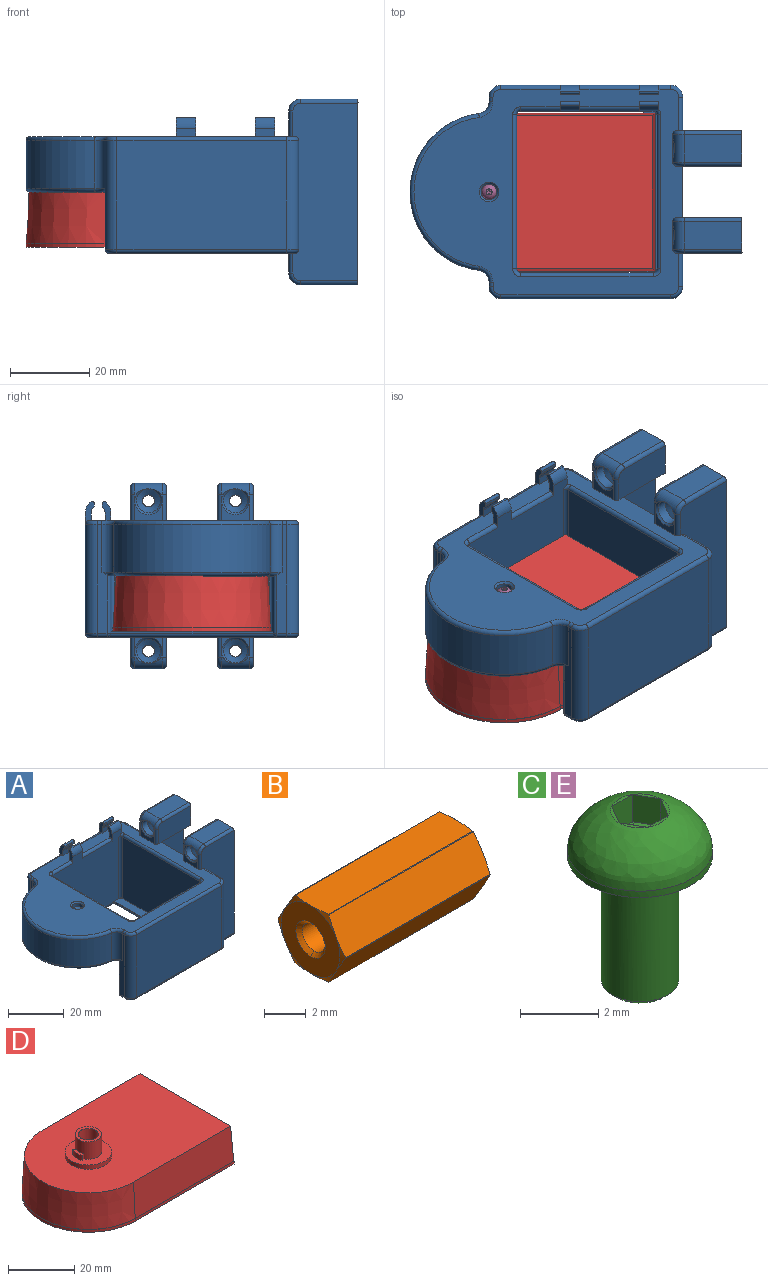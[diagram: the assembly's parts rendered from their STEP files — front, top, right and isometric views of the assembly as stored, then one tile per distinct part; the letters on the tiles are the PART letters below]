
ASSEMBLY  parts=5 mates=4
PART A: 200 faces, bbox 85.7x54.5x47.5 mm
  f0: plane 43x30.5mm, normal (0,1,0), area 1212.5mm2, adj f1,f5,f6,f10,f21,f25,f26,f29
  f1: cylinder r=3.25mm len=5mm, axis (1,0,0), area 16.2mm2, adj f0,f5,f6,f7
  f2: plane 5x0.63mm, normal (0,-1,0), area 3.1mm2, adj f5,f6,f7,f8
  f3: cylinder r=1.75mm len=5mm, axis (1,0,0), area 7.4mm2, adj f4,f5,f6,f8
  f4: plane 5x2mm, normal (0,-1,0), area 10mm2, adj f3,f5,f6,f9
  f5: plane 5.81x2.25mm, normal (-1,0,0), area 7.4mm2, adj f0,f1,f2,f3,f4,f7,f8,f9
  f6: plane 5.81x2.25mm, normal (1,0,0), area 7.4mm2, adj f0,f1,f2,f3,f4,f7,f8,f9
  f7: cylinder r=0.5mm len=5mm, axis (1,0,0), area 5.4mm2, adj f1,f2,f5,f6
  f8: cylinder r=0.5mm len=5mm, axis (1,0,0), area 2.1mm2, adj f2,f3,f5,f6
  f9: plane 68x52mm, normal (0,0,1), area 1399.2mm2, adj f4,f5,f6,f10,f14,f16,f17,f20
  f10: cylinder r=1mm len=15mm, axis (1,0,0), area 23.6mm2, adj f0,f5,f9,f128
  f11: plane 5x0.63mm, normal (0,1,0), area 3.1mm2, adj f16,f17,f18,f19
  f12: cylinder r=3.25mm len=5mm, axis (1,0,0), area 16.2mm2, adj f13,f16,f17,f18
  f13: plane 42x30.5mm, normal (0,-1,0), area 1050.6mm2, adj f12,f16,f17,f20,f31,f34,f35,f38
  f14: plane 5x2mm, normal (0,1,0), area 10mm2, adj f9,f15,f16,f17
  f15: cylinder r=1.75mm len=5mm, axis (1,0,0), area 7.4mm2, adj f14,f16,f17,f19
  f16: plane 5.81x2.25mm, normal (-1,0,0), area 7.4mm2, adj f9,f11,f12,f13,f14,f15,f18,f19
  f17: plane 5.81x2.25mm, normal (1,0,0), area 7.4mm2, adj f9,f11,f12,f13,f14,f15,f18,f19
  f18: cylinder r=0.5mm len=5mm, axis (1,0,0), area 5.4mm2, adj f11,f12,f16,f17
  f19: cylinder r=0.5mm len=5mm, axis (1,0,0), area 2.1mm2, adj f11,f15,f16,f17
  f20: cylinder r=1mm len=10mm, axis (-1,0,0), area 15.7mm2, adj f9,f13,f16,f177
  f21: cylinder r=3.25mm len=5mm, axis (1,0,0), area 16.2mm2, adj f0,f25,f26,f27
  f22: plane 5x0.63mm, normal (0,-1,0), area 3.1mm2, adj f25,f26,f27,f28
  f23: cylinder r=1.75mm len=5mm, axis (1,0,0), area 7.4mm2, adj f24,f25,f26,f28
  f24: plane 5x2mm, normal (0,-1,0), area 10mm2, adj f9,f23,f25,f26
  f25: plane 5.81x2.25mm, normal (-1,0,0), area 7.4mm2, adj f0,f9,f21,f22,f23,f24,f27,f28
  f26: plane 5.81x2.25mm, normal (1,0,0), area 7.4mm2, adj f0,f9,f21,f22,f23,f24,f27,f28
  f27: cylinder r=0.5mm len=5mm, axis (1,0,0), area 5.4mm2, adj f21,f22,f25,f26
  f28: cylinder r=0.5mm len=5mm, axis (1,0,0), area 2.1mm2, adj f22,f23,f25,f26
  f29: cylinder r=1mm len=15mm, axis (1,0,0), area 23.6mm2, adj f0,f6,f9,f25
  f30: plane 5x0.63mm, normal (0,1,0), area 3.1mm2, adj f34,f35,f36,f37
  f31: cylinder r=3.25mm len=5mm, axis (1,0,0), area 16.2mm2, adj f13,f34,f35,f36
  f32: plane 5x2mm, normal (0,1,0), area 10mm2, adj f9,f33,f34,f35
  f33: cylinder r=1.75mm len=5mm, axis (1,0,0), area 7.4mm2, adj f32,f34,f35,f37
  f34: plane 5.81x2.25mm, normal (-1,0,0), area 7.4mm2, adj f9,f13,f30,f31,f32,f33,f36,f37
  f35: plane 4.84x2.27mm, normal (1,0,0), area 7.2mm2, adj f9,f13,f30,f31,f32,f33,f36,f37
  f36: cylinder r=0.5mm len=5mm, axis (1,0,0), area 5.4mm2, adj f30,f31,f34,f35
  f37: cylinder r=0.5mm len=5mm, axis (1,0,0), area 2.1mm2, adj f30,f33,f34,f35
  f38: cylinder r=1mm len=15mm, axis (-1,0,0), area 23.6mm2, adj f9,f13,f17,f34
  f39: cylinder r=1.5mm len=13.6mm, axis (1,0,0), area 128.2mm2, adj f68,f197
  f40: plane 1.5x0.34mm, normal (-1,0,0), area 0.2mm2, adj f43,f150,f199
  f41: plane 3.5x3.5mm, normal (-1,0,0), area 2.6mm2, adj f76,f150,f199
  f42: plane 1.5x0.34mm, normal (-1,0,0), area 0.2mm2, adj f43,f153,f199
  f43: cylinder r=3mm len=7mm, axis (0,-1,0), area 25.5mm2, adj f40,f42,f101,f149,f152,f199
  f44: cylinder r=1.5mm len=13.6mm, axis (1,0,0), area 128.2mm2, adj f71,f196
  f45: plane 1.5x0.34mm, normal (-1,0,0), area 0.2mm2, adj f48,f135,f195
  f46: plane 3.5x3.5mm, normal (-1,0,0), area 2.6mm2, adj f76,f135,f195
  f47: plane 1.5x0.34mm, normal (-1,0,0), area 0.2mm2, adj f48,f132,f195
  f48: cylinder r=3mm len=7mm, axis (0,-1,0), area 25.5mm2, adj f45,f47,f93,f131,f134,f195
  f49: cylinder r=1.5mm len=13.6mm, axis (1,0,0), area 128.2mm2, adj f68,f193
  f50: plane 1.5x0.34mm, normal (-1,0,0), area 0.2mm2, adj f52,f144,f192
  f51: plane 7x5mm, normal (-1,0,0), area 15.8mm2, adj f9,f144,f147,f192
  f52: cylinder r=3mm len=7mm, axis (0,1,0), area 25.5mm2, adj f50,f107,f108,f143,f146,f192
  f53: cylinder r=1.5mm len=13.6mm, axis (1,0,0), area 128.2mm2, adj f71,f188
  f54: plane 1.5x0.34mm, normal (-1,0,0), area 0.2mm2, adj f56,f141,f190
  f55: plane 7x5mm, normal (-1,0,0), area 15.8mm2, adj f9,f138,f141,f190
  f56: cylinder r=3mm len=7mm, axis (0,1,0), area 25.5mm2, adj f54,f99,f100,f137,f140,f190
  f57: cylinder r=1mm len=2mm, axis (0,0,-1), area 8.8mm2, adj f92,f187
  f58: plane 29.5x20mm, normal (1,0,0), area 579.5mm2, adj f9,f69,f70,f76,f95,f96,f98,f103
  f59: plane 4.2x1.37mm, normal (0,0,-1), area 3.9mm2, adj f81,f82,f83,f84
  f60: plane 39x13mm, normal (1,0,0), area 484.6mm2, adj f61,f77,f79,f80,f170,f176,f178
  f61: plane 41.4x27mm, normal (0,0,-1), area 681.3mm2, adj f13,f60,f75,f77,f78,f79,f164,f165
  f62: plane 27.54x2.54mm, normal (-1,0,0), area 52.6mm2, adj f111,f116,f129,f154,f166,f182
  f63: cylinder r=20mm len=39.66mm, axis (0,0,-1), area 691.2mm2, adj f111,f112,f125,f165
  f64: plane 27.54x2.54mm, normal (-1,0,0), area 52.6mm2, adj f112,f113,f121,f159,f164,f179
  f65: plane 43x27.5mm, normal (0,-1,0), area 1182.5mm2, adj f113,f114,f119,f162
  f66: plane 27.5x8.5mm, normal (1,0,0), area 233.7mm2, adj f67,f114,f117,f161
  f67: plane 45x16.5mm, normal (0,-1,0), area 697mm2, adj f9,f66,f68,f76,f117,f145,f146,f147
  f68: plane 47x9mm, normal (1,0,0), area 310mm2, adj f39,f49,f67,f69,f101,f103,f104,f105
  f69: plane 28x15mm, normal (0,1,0), area 420mm2, adj f58,f68,f104,f105
  f70: plane 28x15mm, normal (0,-1,0), area 420mm2, adj f58,f71,f96,f98
  f71: plane 47x9mm, normal (1,0,0), area 310mm2, adj f44,f53,f70,f72,f93,f95,f96,f97
  f72: plane 45x16.5mm, normal (0,1,0), area 697mm2, adj f9,f71,f73,f76,f122,f133,f134,f135
  f73: plane 27.5x8.5mm, normal (1,0,0), area 233.7mm2, adj f72,f115,f122,f157
  f74: plane 39x27mm, normal (-1,0,0), area 1053mm2, adj f110,f168,f172,f173
  f75: plane 40.5x27.5mm, normal (0,1,0), area 1021.5mm2, adj f61,f109,f110,f168,f170,f171,f179,f181
  f76: plane 52x48mm, normal (0,0,-1), area 750.4mm2, adj f41,f46,f58,f67,f72,f94,f95,f102
  f77: plane 7x1.6mm, normal (0,-1,0), area 11.2mm2, adj f60,f61,f78,f80
  f78: cylinder r=7mm len=14mm, axis (0,0,-1), area 35.2mm2, adj f61,f77,f79,f80
  f79: plane 7x1.6mm, normal (0,1,0), area 11.2mm2, adj f60,f61,f78,f80
  f80: plane 14x14mm, normal (0,0,-1), area 120.8mm2, adj f60,f77,f78,f79,f81,f82,f83,f84
  f81: plane 1.9x0.91mm, normal (-0.42,0.91,0), area 1.9mm2, adj f59,f80,f82,f84
  f82: cylinder r=4mm len=8mm, axis (0,0,-1), area 154.3mm2, adj f59,f80,f81,f83,f85
  f83: plane 1.9x0.91mm, normal (-0.42,-0.91,0), area 1.9mm2, adj f59,f80,f82,f84
  f84: cylinder r=5mm len=4.2mm, axis (0,0,-1), area 8.2mm2, adj f59,f80,f81,f83
  f85: plane 8x8mm, normal (0,0,-1), area 32.7mm2, adj f82,f86,f87,f88,f89,f90,f91
  f86: plane 2.13x2mm, normal (-0.82,0.57,0), area 5.2mm2, adj f85,f87,f91,f92
  f87: plane 2.35x2mm, normal (-0.91,-0.42,0), area 5.2mm2, adj f85,f86,f88,f92
  f88: plane 2.59x2mm, normal (-0.09,-1,0), area 5.2mm2, adj f85,f87,f89,f92
  f89: plane 2.13x2mm, normal (0.82,-0.57,0), area 5.2mm2, adj f85,f88,f90,f92
  f90: plane 2.35x2mm, normal (0.91,0.42,0), area 5.2mm2, adj f85,f89,f91,f92
  f91: plane 2.59x2mm, normal (0.09,1,0), area 5.2mm2, adj f85,f86,f90,f92
  f92: plane 5.18x4.71mm, normal (0,0,-1), area 14.4mm2, adj f57,f86,f87,f88,f89,f90,f91
  f93: plane 14.5x7mm, normal (0,0,-1), area 101.5mm2, adj f48,f71,f130,f133
  f94: plane 3.5x3.5mm, normal (-1,0,0), area 2.6mm2, adj f76,f132,f195
  f95: plane 16.5x8.5mm, normal (0,-1,0), area 137.1mm2, adj f58,f71,f76,f96,f130,f131,f132
  f96: plane 15x3.5mm, normal (0,0,1), area 52.5mm2, adj f58,f70,f71,f95
  f97: plane 16.5x8.5mm, normal (0,-1,0), area 139.4mm2, adj f9,f71,f98,f136,f137,f138
  f98: plane 15x3.5mm, normal (0,0,-1), area 52.5mm2, adj f58,f70,f71,f97
  f99: plane 14.5x7mm, normal (0,0,1), area 101.5mm2, adj f56,f71,f136,f139
  f100: plane 1.5x0.34mm, normal (-1,0,0), area 0.2mm2, adj f56,f138,f190
  f101: plane 14.5x7mm, normal (0,0,-1), area 101.5mm2, adj f43,f68,f148,f151
  f102: plane 3.5x3.5mm, normal (-1,0,0), area 2.6mm2, adj f76,f153,f199
  f103: plane 16.5x8.5mm, normal (0,1,0), area 137.1mm2, adj f58,f68,f76,f104,f148,f149,f150
  f104: plane 15x3.5mm, normal (0,0,1), area 52.5mm2, adj f58,f68,f69,f103
  f105: plane 15x3.5mm, normal (0,0,-1), area 52.5mm2, adj f58,f68,f69,f106
  f106: plane 16.5x8.5mm, normal (0,1,0), area 139.4mm2, adj f9,f68,f105,f142,f143,f144
  f107: plane 14.5x7mm, normal (0,0,1), area 101.5mm2, adj f52,f68,f142,f145
  f108: plane 1.5x0.34mm, normal (-1,0,0), area 0.2mm2, adj f52,f147,f192
  f109: plane 41x0.5mm, normal (-1,0,0), area 20.5mm2, adj f13,f75,f110,f167
  f110: plane 41x3.5mm, normal (0,0,1), area 143.1mm2, adj f13,f74,f75,f109,f168,f173
  f111: cylinder r=3mm len=12mm, axis (0,0,-1), area 51.8mm2, adj f62,f63,f127,f166
  f112: cylinder r=3mm len=12mm, axis (0,0,-1), area 51.8mm2, adj f63,f64,f123,f164
  f113: cylinder r=3mm len=27.5mm, axis (0,0,-1), area 129.6mm2, adj f64,f65,f120,f160
  f114: cylinder r=3mm len=27.5mm, axis (0,0,-1), area 129.6mm2, adj f65,f66,f118,f163
  f115: cylinder r=3mm len=27.5mm, axis (0,0,-1), area 129.6mm2, adj f0,f73,f124,f158
  f116: cylinder r=3mm len=27.5mm, axis (0,0,-1), area 129.6mm2, adj f0,f62,f128,f155
  f117: cylinder r=1mm len=8.5mm, axis (0,-1,0), area 13.4mm2, adj f9,f66,f67,f118
  f118: torus R=2mm, axis (0,0,1), area 6.5mm2, adj f9,f114,f117,f119
  f119: cylinder r=1mm len=43mm, axis (-1,0,0), area 67.5mm2, adj f9,f65,f118,f120
  f120: torus R=2mm, axis (0,0,1), area 6.5mm2, adj f9,f113,f119,f121
  f121: cylinder r=1mm len=1.2mm, axis (0,1,0), area 1.9mm2, adj f9,f64,f120,f123
  f122: cylinder r=1mm len=8.5mm, axis (0,-1,0), area 13.4mm2, adj f9,f72,f73,f124
  f123: torus R=4mm, axis (0,0,1), area 7.6mm2, adj f9,f112,f121,f125
  f124: torus R=2mm, axis (0,0,1), area 6.5mm2, adj f9,f115,f122,f126
  f125: torus R=19mm, axis (0,0,1), area 88.8mm2, adj f9,f63,f123,f127
  f126: cylinder r=1mm len=3mm, axis (1,0,0), area 4.7mm2, adj f0,f9,f26,f124
  f127: torus R=4mm, axis (0,0,1), area 7.6mm2, adj f9,f111,f125,f129
  f128: torus R=2mm, axis (0,0,1), area 6.5mm2, adj f9,f10,f116,f129
  f129: cylinder r=1mm len=1.2mm, axis (0,1,0), area 1.9mm2, adj f9,f62,f127,f128
  f130: cylinder r=1mm len=14.5mm, axis (-1,0,0), area 22.8mm2, adj f71,f93,f95,f131
  f131: torus R=2mm, axis (0,-1,0), area 6.5mm2, adj f48,f95,f130,f132
  f132: cylinder r=1mm len=5mm, axis (0,0,1), area 7.9mm2, adj f47,f76,f94,f95,f131
  f133: cylinder r=1mm len=14.5mm, axis (-1,0,0), area 22.8mm2, adj f71,f72,f93,f134
  f134: torus R=2mm, axis (0,1,0), area 6.5mm2, adj f48,f72,f133,f135
  f135: cylinder r=1mm len=5mm, axis (0,0,-1), area 7.9mm2, adj f45,f46,f72,f76,f134
  f136: cylinder r=1mm len=14.5mm, axis (-1,0,0), area 22.8mm2, adj f71,f97,f99,f137
  f137: torus R=2mm, axis (0,1,0), area 6.5mm2, adj f56,f97,f136,f138
  f138: cylinder r=1mm len=6.5mm, axis (0,0,1), area 10.2mm2, adj f9,f55,f97,f100,f137
  f139: cylinder r=1mm len=14.5mm, axis (1,0,0), area 22.8mm2, adj f71,f72,f99,f140
  f140: torus R=2mm, axis (0,1,0), area 6.5mm2, adj f56,f72,f139,f141
  f141: cylinder r=1mm len=6.5mm, axis (0,0,-1), area 10.2mm2, adj f9,f54,f55,f72,f140
  f142: cylinder r=1mm len=14.5mm, axis (-1,0,0), area 22.8mm2, adj f68,f106,f107,f143
  f143: torus R=2mm, axis (0,1,0), area 6.5mm2, adj f52,f106,f142,f144
  f144: cylinder r=1mm len=6.5mm, axis (0,0,-1), area 10.2mm2, adj f9,f50,f51,f106,f143
  f145: cylinder r=1mm len=14.5mm, axis (1,0,0), area 22.8mm2, adj f67,f68,f107,f146
  f146: torus R=2mm, axis (0,1,0), area 6.5mm2, adj f52,f67,f145,f147
  f147: cylinder r=1mm len=6.5mm, axis (0,0,-1), area 10.2mm2, adj f9,f51,f67,f108,f146
  f148: cylinder r=1mm len=14.5mm, axis (-1,0,0), area 22.8mm2, adj f68,f101,f103,f149
  f149: torus R=2mm, axis (0,-1,0), area 6.5mm2, adj f43,f103,f148,f150
  f150: cylinder r=1mm len=5mm, axis (0,0,-1), area 7.9mm2, adj f40,f41,f76,f103,f149
  f151: cylinder r=1mm len=14.5mm, axis (-1,0,0), area 22.8mm2, adj f67,f68,f101,f152
  f152: torus R=2mm, axis (0,1,0), area 6.5mm2, adj f43,f67,f151,f153
  f153: cylinder r=1mm len=5mm, axis (0,0,-1), area 7.9mm2, adj f42,f67,f76,f102,f152
  f154: cylinder r=1mm len=2.5mm, axis (0,-1,0), area 3.9mm2, adj f62,f76,f155,f183
  f155: torus R=2mm, axis (0,0,1), area 6.5mm2, adj f76,f116,f154,f156
  f156: cylinder r=1mm len=43mm, axis (-1,0,0), area 67.5mm2, adj f0,f76,f155,f158
  f157: cylinder r=1mm len=8.5mm, axis (0,1,0), area 13.4mm2, adj f72,f73,f76,f158
  f158: torus R=2mm, axis (0,0,1), area 6.5mm2, adj f76,f115,f156,f157
  f159: cylinder r=1mm len=2.5mm, axis (0,-1,0), area 3.9mm2, adj f64,f76,f160,f180
  f160: torus R=2mm, axis (0,0,1), area 6.5mm2, adj f76,f113,f159,f162
  f161: cylinder r=1mm len=8.5mm, axis (0,1,0), area 13.4mm2, adj f66,f67,f76,f163
  f162: cylinder r=1mm len=43mm, axis (1,0,0), area 67.5mm2, adj f65,f76,f160,f163
  f163: torus R=2mm, axis (0,0,1), area 6.5mm2, adj f76,f114,f161,f162
  f164: torus R=4mm, axis (0,0,1), area 5.6mm2, adj f61,f64,f112,f165,f179
  f165: torus R=19mm, axis (0,0,1), area 88.8mm2, adj f61,f63,f164,f166
  f166: torus R=4mm, axis (0,0,1), area 5.6mm2, adj f61,f62,f111,f165,f182
  f167: cylinder r=1mm len=43mm, axis (0,1,0), area 65.5mm2, adj f76,f109,f181,f184
  f168: cylinder r=1mm len=27mm, axis (0,0,-1), area 42.4mm2, adj f74,f75,f110,f169
  f169: torus R=2mm, axis (0,0,1), area 3.4mm2, adj f9,f168,f171,f172
  f170: cylinder r=1mm len=13mm, axis (0,0,1), area 20.4mm2, adj f60,f61,f75,f174
  f171: cylinder r=1mm len=33.5mm, axis (1,0,0), area 52.6mm2, adj f9,f75,f169,f174
  f172: cylinder r=1mm len=39mm, axis (0,1,0), area 61.3mm2, adj f9,f74,f169,f175
  f173: cylinder r=1mm len=27mm, axis (0,0,1), area 42.4mm2, adj f13,f74,f110,f175
  f174: torus R=2mm, axis (0,0,1), area 3.4mm2, adj f9,f170,f171,f176
  f175: torus R=2mm, axis (0,0,1), area 1.9mm2, adj f9,f13,f35,f172,f173
  f176: cylinder r=1mm len=39mm, axis (0,-1,0), area 61.3mm2, adj f9,f60,f174,f177
  f177: torus R=2mm, axis (0,0,1), area 3.4mm2, adj f9,f20,f176,f178
  f178: cylinder r=1mm len=13mm, axis (0,0,-1), area 20.4mm2, adj f13,f60,f61,f177
  f179: cylinder r=1mm len=14.82mm, axis (0,0,-1), area 22.9mm2, adj f61,f64,f75,f164,f180
  f180: sphere r=1mm, area 1.6mm2, adj f159,f179,f181
  f181: cylinder r=1mm len=39mm, axis (-1,0,0), area 60.3mm2, adj f75,f76,f167,f180
  f182: cylinder r=1mm len=14.82mm, axis (0,0,-1), area 22.9mm2, adj f13,f61,f62,f166,f183
  f183: sphere r=1mm, area 1.6mm2, adj f154,f182,f184
  f184: cylinder r=1mm len=39mm, axis (1,0,0), area 60.3mm2, adj f13,f76,f167,f183
  f185: cylinder r=2mm len=4mm, axis (0,0,1), area 18.8mm2, adj f186,f187
  f186: cone r=2mm half-angle=45deg, axis (0,0,1), area 10mm2, adj f9,f185
  f187: cone r=0mm half-angle=59deg, axis (0,0,1), area 11mm2, adj f57,f185
  f188: cone r=0mm half-angle=59deg, axis (-1,0,0), area 24.7mm2, adj f53,f189
  f189: cylinder r=3mm len=6mm, axis (-1,0,0), area 47.1mm2, adj f188,f190
  f190: cone r=3mm half-angle=45deg, axis (-1,0,0), area 11.9mm2, adj f54,f55,f56,f100,f189
  f191: cylinder r=3mm len=6mm, axis (-1,0,0), area 47.1mm2, adj f192,f193
  f192: cone r=3mm half-angle=45deg, axis (-1,0,0), area 11.9mm2, adj f50,f51,f52,f108,f191
  f193: cone r=0mm half-angle=59deg, axis (-1,0,0), area 24.7mm2, adj f49,f191
  f194: cylinder r=3mm len=6mm, axis (-1,0,0), area 47.1mm2, adj f195,f196
  f195: cone r=3mm half-angle=45deg, axis (-1,0,0), area 11.8mm2, adj f45,f46,f47,f48,f94,f194
  f196: cone r=0mm half-angle=59deg, axis (-1,0,0), area 24.7mm2, adj f44,f194
  f197: cone r=0mm half-angle=59deg, axis (-1,0,0), area 24.7mm2, adj f39,f198
  f198: cylinder r=3mm len=6mm, axis (-1,0,0), area 47.1mm2, adj f197,f199
  f199: cone r=3mm half-angle=45deg, axis (-1,0,0), area 11.8mm2, adj f40,f41,f42,f43,f102,f198
PART B: 31 faces, bbox 10x4.6x4.6 mm
  f0: cone r=1mm half-angle=45deg, axis (-1,0,0), area 0.9mm2, adj f1,f2,f3
  f1: cone r=1mm half-angle=45deg, axis (-1,0,0), area 0.9mm2, adj f0,f2,f3
  f2: cylinder r=0.78mm len=9.57mm, axis (-1,0,0), area 47.1mm2, adj f0,f1,f27,f28
  f3: plane 4x4mm, normal (-1,0,0), area 9.4mm2, adj f0,f1,f4,f5,f6,f7,f8,f9
  f4: cone r=2mm half-angle=75deg, axis (1,0,0), area 0.2mm2, adj f3,f17,f18,f20
  f5: cone r=2mm half-angle=75deg, axis (1,0,0), area 0.2mm2, adj f3,f15,f16,f17
  f6: cone r=2mm half-angle=75deg, axis (1,0,0), area 0.2mm2, adj f3,f13,f14,f15
  f7: cone r=2mm half-angle=75deg, axis (1,0,0), area 0.2mm2, adj f3,f11,f12,f13
  f8: cone r=2mm half-angle=75deg, axis (1,0,0), area 0.2mm2, adj f3,f10,f11,f21
  f9: cone r=2mm half-angle=75deg, axis (1,0,0), area 0.2mm2, adj f3,f19,f20,f21
  f10: cylinder r=2.3mm len=9.84mm, axis (-1,0,0), area 0.3mm2, adj f8,f11,f21,f26
  f11: plane 10x1.97mm, normal (0,0.87,0.5), area 22.6mm2, adj f7,f8,f10,f12,f26,f29
  f12: cylinder r=2.3mm len=9.84mm, axis (-1,0,0), area 0.3mm2, adj f7,f11,f13,f29
  f13: plane 10x1.97mm, normal (0,0.87,-0.5), area 22.6mm2, adj f6,f7,f12,f14,f25,f29
  f14: cylinder r=2.3mm len=9.84mm, axis (-1,0,0), area 0.3mm2, adj f6,f13,f15,f25
  f15: plane 10x2.27mm, normal (0,0,-1), area 22.6mm2, adj f5,f6,f14,f16,f24,f25
  f16: cylinder r=2.3mm len=9.84mm, axis (-1,0,0), area 0.3mm2, adj f5,f15,f17,f24
  f17: plane 10x1.97mm, normal (0,-0.87,-0.5), area 22.6mm2, adj f4,f5,f16,f18,f22,f24
  f18: cylinder r=2.3mm len=9.84mm, axis (-1,0,0), area 0.3mm2, adj f4,f17,f20,f22
  f19: cylinder r=2.3mm len=9.84mm, axis (-1,0,0), area 0.3mm2, adj f9,f20,f21,f30
  f20: plane 10x1.97mm, normal (0,-0.87,0.5), area 22.6mm2, adj f4,f9,f18,f19,f22,f30
  f21: plane 10x2.27mm, normal (0,0,1), area 22.6mm2, adj f8,f9,f10,f19,f26,f30
  f22: cone r=2.3mm half-angle=75deg, axis (-1,0,0), area 0.2mm2, adj f17,f18,f20,f23
  f23: plane 4x4mm, normal (1,0,0), area 9.4mm2, adj f22,f24,f25,f26,f27,f28,f29,f30
  f24: cone r=2.3mm half-angle=75deg, axis (-1,0,0), area 0.2mm2, adj f15,f16,f17,f23
  f25: cone r=2.3mm half-angle=75deg, axis (-1,0,0), area 0.2mm2, adj f13,f14,f15,f23
  f26: cone r=2.3mm half-angle=75deg, axis (-1,0,0), area 0.2mm2, adj f10,f11,f21,f23
  f27: cone r=0.78mm half-angle=45deg, axis (1,0,0), area 0.9mm2, adj f2,f23,f28
  f28: cone r=0.78mm half-angle=45deg, axis (1,0,0), area 0.9mm2, adj f2,f23,f27
  f29: cone r=2.3mm half-angle=75deg, axis (-1,0,0), area 0.2mm2, adj f11,f12,f13,f23
  f30: cone r=2.3mm half-angle=75deg, axis (-1,0,0), area 0.2mm2, adj f19,f20,f21,f23
PART C: 24 faces, bbox 3.7x3.7x5.4 mm
  f0: plane 0.75x0.1mm, normal (0,0,1), area 0.1mm2, adj f6,f13
  f1: plane 0.65x0.38mm, normal (0,0,1), area 0.1mm2, adj f6,f18
  f2: plane 0.65x0.38mm, normal (0,0,1), area 0.1mm2, adj f6,f17
  f3: plane 0.75x0.1mm, normal (0,0,1), area 0.1mm2, adj f6,f16
  f4: plane 0.65x0.38mm, normal (0,0,1), area 0.1mm2, adj f6,f15
  f5: plane 0.65x0.38mm, normal (0,0,1), area 0.1mm2, adj f6,f14
  f6: bspline ~3.7x3.7mm, area 15.5mm2, adj f0,f1,f2,f3,f4,f5,f19
  f7: plane 0.75x0.65mm, normal (-0.11,0.06,0.99), area 0.2mm2, adj f8,f12,f15
  f8: plane 0.75x0.65mm, normal (0,0.13,0.99), area 0.2mm2, adj f7,f9,f16
  f9: plane 0.75x0.65mm, normal (0.11,0.06,0.99), area 0.2mm2, adj f8,f10,f17
  f10: plane 0.75x0.65mm, normal (0.11,-0.06,0.99), area 0.2mm2, adj f9,f11,f18
  f11: plane 0.75x0.65mm, normal (0,-0.13,0.99), area 0.2mm2, adj f10,f12,f13
  f12: plane 0.75x0.65mm, normal (-0.11,-0.06,0.99), area 0.2mm2, adj f7,f11,f14
  f13: plane 0.85x0.75mm, normal (0,-1,0), area 0.6mm2, adj f0,f11,f14,f18
  f14: plane 0.85x0.65mm, normal (-0.87,-0.5,0), area 0.6mm2, adj f5,f12,f13,f15
  f15: plane 0.85x0.65mm, normal (-0.87,0.5,0), area 0.6mm2, adj f4,f7,f14,f16
  f16: plane 0.85x0.75mm, normal (0,1,0), area 0.6mm2, adj f3,f8,f15,f17
  f17: plane 0.85x0.65mm, normal (0.87,0.5,0), area 0.6mm2, adj f2,f9,f16,f18
  f18: plane 0.85x0.65mm, normal (0.87,-0.5,0), area 0.6mm2, adj f1,f10,f13,f17
  f19: cylinder r=1.85mm len=3.7mm, axis (0,0,-1), area 2.3mm2, adj f6,f20
  f20: plane 3.7x3.7mm, normal (0,0,-1), area 7.7mm2, adj f19,f21
  f21: cylinder r=0.99mm len=3.86mm, axis (0,0,1), area 24mm2, adj f20,f23
  f22: plane 1.7x1.7mm, normal (0,0,-1), area 2.3mm2, adj f23
  f23: cone r=0.85mm half-angle=45deg, axis (0,0,1), area 1.1mm2, adj f21,f22
PART D: 35 faces, bbox 62x40x22 mm
  f0: plane 59.89x37.89mm, normal (0,0,1), area 2115.4mm2, adj f2,f3,f4,f5
  f1: plane 58.63x36.63mm, normal (0,0,-1), area 2000.9mm2, adj f2,f3,f4,f5,f6
  f2: plane 37.89x12mm, normal (-1,0,-0.05), area 447.8mm2, adj f0,f1,f3,f5
  f3: plane 40.95x12mm, normal (0,1,-0.05), area 488.3mm2, adj f0,f1,f2,f4
  f4: cone r=19mm half-angle=3deg, axis (0,0,-1), area 703.4mm2, adj f0,f1,f3,f5
  f5: plane 40.95x12mm, normal (0,-1,-0.05), area 488.3mm2, adj f0,f1,f2,f4
  f6: cylinder r=1mm len=2mm, axis (0,0,1), area 6.3mm2, adj f1,f22
  f7: plane 60.53x38.53mm, normal (0,0,1), area 2019.2mm2, adj f8,f9,f10,f11,f12
  f8: plane 41.95x13mm, normal (0,1,0.05), area 541.6mm2, adj f7,f9,f11,f33
  f9: cone r=20mm half-angle=3deg, axis (0,0,-1), area 801.9mm2, adj f7,f8,f10,f33
  f10: plane 41.95x13mm, normal (0,-1,0.05), area 541.6mm2, adj f7,f9,f11,f33
  f11: plane 39.9x13mm, normal (1,0,0.05), area 510.5mm2, adj f7,f8,f10,f33
  f12: cylinder r=7mm len=14mm, axis (0,0,-1), area 70.4mm2, adj f7,f13
  f13: plane 14x14mm, normal (0,0,1), area 99.8mm2, adj f12,f14,f15,f16,f18
  f14: cylinder r=5mm len=4.2mm, axis (0,0,-1), area 8.2mm2, adj f13,f15,f16,f17
  f15: plane 1.9x0.91mm, normal (0.42,-0.91,0), area 1.9mm2, adj f13,f14,f17,f18
  f16: plane 1.9x0.91mm, normal (0.42,0.91,0), area 1.9mm2, adj f13,f14,f17,f18
  f17: plane 4.2x1.37mm, normal (0,0,1), area 3.9mm2, adj f14,f15,f16,f18
  f18: cylinder r=4mm len=8mm, axis (0,0,-1), area 154.3mm2, adj f13,f15,f16,f17,f19
  f19: plane 8x8mm, normal (0,0,1), area 22mm2, adj f18,f21
  f20: plane 6x6mm, normal (0,0,1), area 10.7mm2, adj f21,f23,f24,f25,f26,f27,f28
  f21: cylinder r=3mm len=6.4mm, axis (0,0,1), area 120.6mm2, adj f19,f20
  f22: plane 5.18x4.71mm, normal (0,0,1), area 14.4mm2, adj f6,f23,f24,f25,f26,f27,f28
  f23: plane 2.59x1.6mm, normal (0.09,1,0), area 4.2mm2, adj f20,f22,f24,f28
  f24: plane 2.35x1.6mm, normal (0.91,0.42,0), area 4.2mm2, adj f20,f22,f23,f25
  f25: plane 2.13x1.6mm, normal (0.82,-0.57,0), area 4.2mm2, adj f20,f22,f24,f26
  f26: plane 2.59x1.6mm, normal (-0.09,-1,0), area 4.2mm2, adj f20,f22,f25,f27
  f27: plane 2.35x1.6mm, normal (-0.91,-0.42,0), area 4.2mm2, adj f20,f22,f26,f28
  f28: plane 2.13x1.6mm, normal (-0.82,0.57,0), area 4.2mm2, adj f20,f22,f23,f27
  f29: plane 42x1mm, normal (0,1,0), area 42mm2, adj f30,f32,f33,f34
  f30: cylinder r=20mm len=40mm, axis (0,0,-1), area 62.8mm2, adj f29,f31,f33,f34
  f31: plane 42x1mm, normal (0,-1,0), area 42mm2, adj f30,f32,f33,f34
  f32: plane 40x1mm, normal (1,0,0), area 40mm2, adj f29,f31,f33,f34
  f33: plane 62x40mm, normal (0,0,1), area 9.8mm2, adj f8,f9,f10,f11,f29,f30,f31,f32
  f34: plane 62x40mm, normal (0,0,-1), area 2308.3mm2, adj f29,f30,f31,f32
PART E: same geometry as C
PLACE A rot(axis=(0.98,0.04,0.18),0deg) t=(-17.97,9.24,64.87)mm
PLACE B rot(axis=(0,-1,0),90deg) t=(-17.97,9.24,64.87)mm
PLACE C rot(axis=(-1,0,0),180deg) t=(-17.97,9.24,62.47)mm
PLACE D rot(axis=(0.98,0.04,0.18),0deg) t=(-17.97,9.24,50.87)mm
PLACE E rot(axis=(0.98,0.04,0.18),0deg) t=(-17.97,9.24,78.27)mm
MATE fastened C.f19 <-> D.f6  axis (0,0,1) through (-17.97,9.24,63.87)mm
MATE fastened D.f4 <-> B.f0  axis (0,0,1) through (-17.97,9.24,64.87)mm
MATE fastened B.f0 <-> A.f57  axis (0,0,1) through (-17.97,9.24,74.87)mm
MATE fastened E.f19 <-> A.f185  axis (0,0,-1) through (-17.97,9.24,76.87)mm
